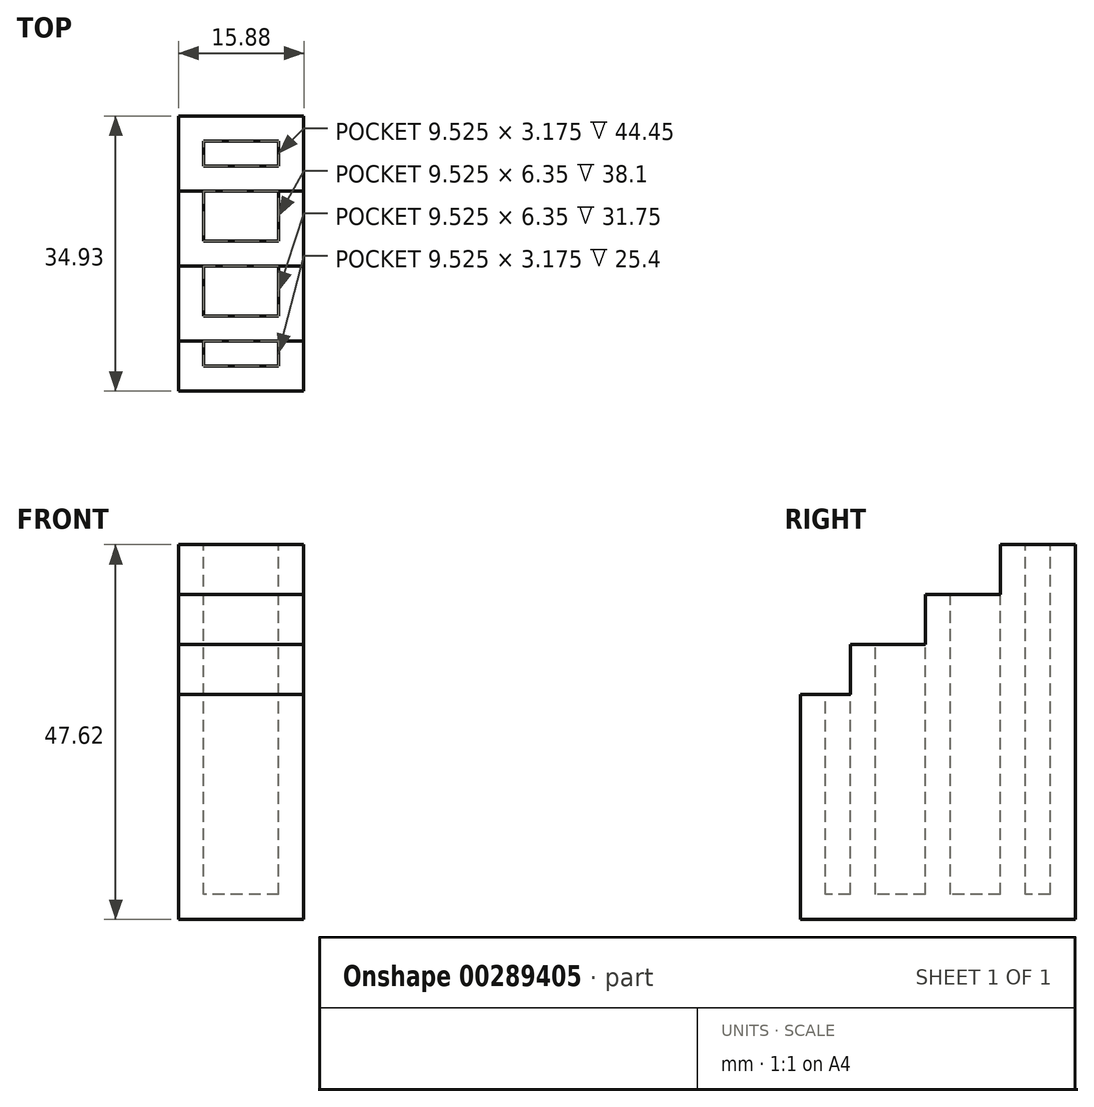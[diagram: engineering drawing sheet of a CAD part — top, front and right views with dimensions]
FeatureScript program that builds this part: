
annotation { "Feature Type Name" : "Feature", "Feature Type Description" : "" }
export const myFeature = defineFeature(function(context is Context, id is Id, definition is map)
    precondition{}
    {
        {
            var Q0;
            Q0=qCreatedBy(makeId("Right.planeOp"),FACE);
            var sketch = newSketch(context, id + "F0", { "sketchPlane" : qUnion([Q0])});
            skLineSegment(sketch, "E0.bottom", {"start": v(-15.06, -7.17) * mm, "end": v(19.87, -7.17) * mm});
            skLineSegment(sketch, "E0.top", {"start": v(-15.06, 40.45) * mm, "end": v(19.87, 40.45) * mm});
            skLineSegment(sketch, "E0.left", {"start": v(-15.06, -7.17) * mm, "end": v(-15.06, 40.45) * mm});
            skLineSegment(sketch, "E0.right", {"start": v(19.87, -7.17) * mm, "end": v(19.87, 40.45) * mm});
            skSolve(sketch);
        }
        {
            var Q0;
            Q0 = qSketchRegion(id + "F0", true);
            extrude(context, id + "F1", {"entities" : qUnion([Q0]), "endBound" : BoundingType.SYMMETRIC, "depth" : 15.88 * mm});
        }
        {
            var Q0;
            Q0=qCreatedBy(makeId("Right.planeOp"),FACE);
            var sketch = newSketch(context, id + "F2", { "sketchPlane" : qUnion([Q0])});
            skLineSegment(sketch, "E1", {"start": v(-15.06, 21.4) * mm, "end": v(-8.7, 21.4) * mm});
            skLineSegment(sketch, "E2", {"start": v(-8.7, 21.4) * mm, "end": v(-8.7, 27.75) * mm});
            skLineSegment(sketch, "E3", {"start": v(-8.7, 27.75) * mm, "end": v(0.82, 27.75) * mm});
            skLineSegment(sketch, "E4", {"start": v(0.82, 27.75) * mm, "end": v(0.82, 34.1) * mm});
            skLineSegment(sketch, "E5", {"start": v(0.82, 34.1) * mm, "end": v(10.34, 34.1) * mm});
            skLineSegment(sketch, "E6", {"start": v(10.34, 34.1) * mm, "end": v(10.34, 40.45) * mm});
            skLineSegment(sketch, "E7", {"start": v(10.34, 40.45) * mm, "end": v(19.87, 40.45) * mm});
            skLineSegment(sketch, "E8", {"start": v(19.87, 40.45) * mm, "end": v(19.87, 46.8) * mm});
            skLineSegment(sketch, "E9", {"start": v(-15.06, 21.4) * mm, "end": v(-15.06, 46.8) * mm});
            skLineSegment(sketch, "E10", {"start": v(19.87, 46.8) * mm, "end": v(-15.06, 46.8) * mm});
            skSolve(sketch);
        }
        {
            var Q0;
            Q0 = qSketchRegion(id + "F2", true);
            extrude(context, id + "F3", {"entities" : qUnion([Q0]), "operationType" : NewBodyOperationType.REMOVE, "endBound" : BoundingType.SYMMETRIC, "depth" : 25.4 * mm});
        }
        {
            var Q0;
            Q0=makeQuery(id+"F1.opExtrude","SWEPT_FACE",FACE,{"disambiguationData":[OSD([sQuery(id+"F0.wireOp",EDGE,"E0.top")])]});
            var sketch = newSketch(context, id + "F4", { "sketchPlane" : qUnion([Q0])});
            skLineSegment(sketch, "E11.bottom", {"start": v(-4.76, 16.7) * mm, "end": v(4.76, 16.7) * mm});
            skLineSegment(sketch, "E11.top", {"start": v(-4.76, 13.52) * mm, "end": v(4.76, 13.52) * mm});
            skLineSegment(sketch, "E11.left", {"start": v(-4.76, 16.7) * mm, "end": v(-4.76, 13.52) * mm});
            skLineSegment(sketch, "E11.right", {"start": v(4.76, 16.7) * mm, "end": v(4.76, 13.52) * mm});
            skSolve(sketch);
        }
        {
            var Q0;
            Q0=makeQuery(id+"F4.imprint","IMPRINT",FACE,{"disambiguationData":[TD([[makeQuery(id+"F4.imprint","IMPRINT",EDGE,{"derivedFrom":sQuery(id+"F4.wireOp",EDGE,"E11.bottom")}),-1.0]])]});
            extrude(context, id + "F5", {"entities" : qUnion([Q0]), "operationType" : NewBodyOperationType.REMOVE, "oppositeDirection" : true, "depth" : 44.45 * mm});
        }
        {
            var Q0;
            Q0=makeQuery(id+"F3.boolean.opBoolean","COPY",FACE,{"derivedFrom":makeQuery(id+"F3.opExtrude","SWEPT_FACE",FACE,{"disambiguationData":[OSD([sQuery(id+"F2.wireOp",EDGE,"E5")])]})});
            var sketch = newSketch(context, id + "F6", { "sketchPlane" : qUnion([Q0])});
            skLineSegment(sketch, "E12.bottom", {"start": v(-4.76, 10.34) * mm, "end": v(4.76, 10.34) * mm});
            skLineSegment(sketch, "E12.top", {"start": v(-4.76, 4) * mm, "end": v(4.76, 4) * mm});
            skLineSegment(sketch, "E12.left", {"start": v(-4.76, 10.34) * mm, "end": v(-4.76, 4) * mm});
            skLineSegment(sketch, "E12.right", {"start": v(4.76, 10.34) * mm, "end": v(4.76, 4) * mm});
            skSolve(sketch);
        }
        {
            var Q0;
            Q0=makeQuery(id+"F6.imprint","IMPRINT",FACE,{"disambiguationData":[TD([[makeQuery(id+"F6.imprint","IMPRINT",EDGE,{"derivedFrom":sQuery(id+"F6.wireOp",EDGE,"E12.bottom")}),1.0]])]});
            extrude(context, id + "F7", {"entities" : qUnion([Q0]), "operationType" : NewBodyOperationType.REMOVE, "oppositeDirection" : true, "depth" : 38.1 * mm});
        }
        {
            var Q0;
            Q0=makeQuery(id+"F3.boolean.opBoolean","COPY",FACE,{"derivedFrom":makeQuery(id+"F3.opExtrude","SWEPT_FACE",FACE,{"disambiguationData":[OSD([sQuery(id+"F2.wireOp",EDGE,"E3")])]})});
            var sketch = newSketch(context, id + "F8", { "sketchPlane" : qUnion([Q0])});
            skLineSegment(sketch, "E13.bottom", {"start": v(-4.76, 0.82) * mm, "end": v(4.76, 0.82) * mm});
            skLineSegment(sketch, "E13.top", {"start": v(-4.76, -5.53) * mm, "end": v(4.76, -5.53) * mm});
            skLineSegment(sketch, "E13.left", {"start": v(-4.76, 0.82) * mm, "end": v(-4.76, -5.53) * mm});
            skLineSegment(sketch, "E13.right", {"start": v(4.76, 0.82) * mm, "end": v(4.76, -5.53) * mm});
            skSolve(sketch);
        }
        {
            var Q0;
            Q0=makeQuery(id+"F8.imprint","IMPRINT",FACE,{"disambiguationData":[TD([[makeQuery(id+"F8.imprint","IMPRINT",EDGE,{"derivedFrom":sQuery(id+"F8.wireOp",EDGE,"E13.bottom")}),1.0]])]});
            extrude(context, id + "F9", {"entities" : qUnion([Q0]), "operationType" : NewBodyOperationType.REMOVE, "oppositeDirection" : true, "depth" : 31.75 * mm});
        }
        {
            var Q0;
            Q0=makeQuery(id+"F3.boolean.opBoolean","COPY",FACE,{"derivedFrom":makeQuery(id+"F3.opExtrude","SWEPT_FACE",FACE,{"disambiguationData":[OSD([sQuery(id+"F2.wireOp",EDGE,"E1")])]})});
            var sketch = newSketch(context, id + "F10", { "sketchPlane" : qUnion([Q0])});
            skLineSegment(sketch, "E14.bottom", {"start": v(-4.76, -8.7) * mm, "end": v(4.76, -8.7) * mm});
            skLineSegment(sketch, "E14.top", {"start": v(-4.76, -11.88) * mm, "end": v(4.76, -11.88) * mm});
            skLineSegment(sketch, "E14.left", {"start": v(-4.76, -8.7) * mm, "end": v(-4.76, -11.88) * mm});
            skLineSegment(sketch, "E14.right", {"start": v(4.76, -8.7) * mm, "end": v(4.76, -11.88) * mm});
            skSolve(sketch);
        }
        {
            var Q0;
            Q0=makeQuery(id+"F10.imprint","IMPRINT",FACE,{"disambiguationData":[TD([[makeQuery(id+"F10.imprint","IMPRINT",EDGE,{"derivedFrom":sQuery(id+"F10.wireOp",EDGE,"E14.bottom")}),1.0]])]});
            extrude(context, id + "F11", {"entities" : qUnion([Q0]), "operationType" : NewBodyOperationType.REMOVE, "oppositeDirection" : true, "depth" : 25.4 * mm});
        }
    });
